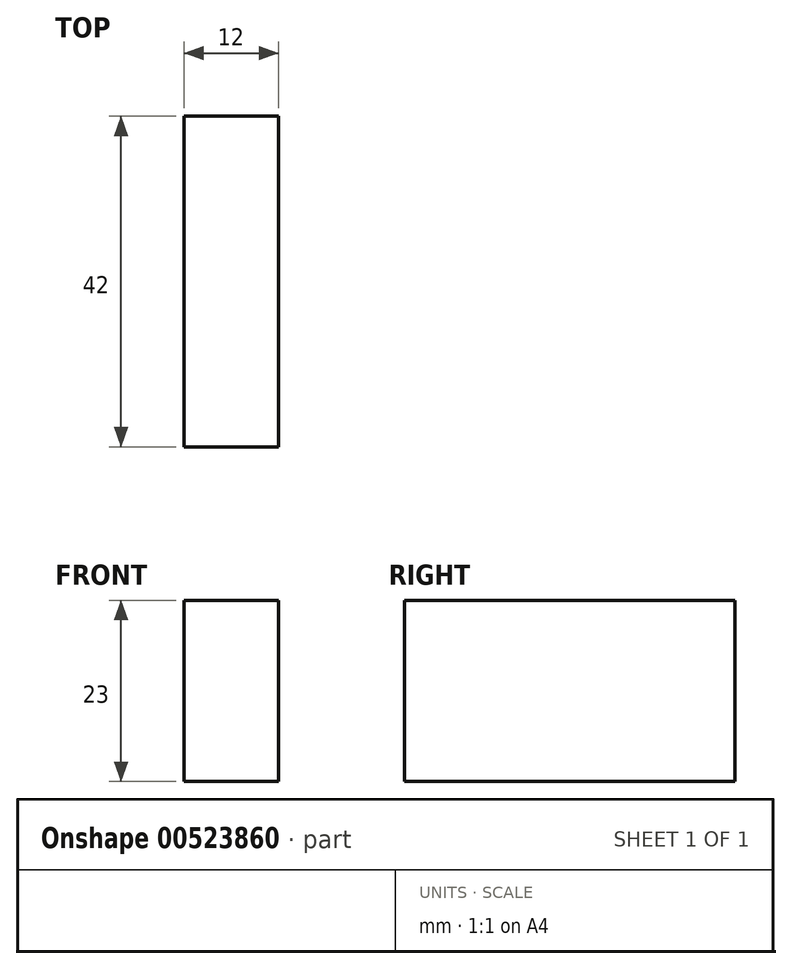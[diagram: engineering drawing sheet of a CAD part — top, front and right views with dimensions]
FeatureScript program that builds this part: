
annotation { "Feature Type Name" : "Feature", "Feature Type Description" : "" }
export const myFeature = defineFeature(function(context is Context, id is Id, definition is map)
    precondition{}
    {
        {
            var Q0;
            Q0=qCreatedBy(makeId("Right.planeOp"),FACE);
            var sketch = newSketch(context, id + "F0", { "sketchPlane" : qUnion([Q0])});
            skLineSegment(sketch, "E0.bottom", {"start": v(-21, 11.5) * mm, "end": v(21, 11.5) * mm});
            skLineSegment(sketch, "E0.top", {"start": v(-21, -11.5) * mm, "end": v(21, -11.5) * mm});
            skLineSegment(sketch, "E0.left", {"start": v(-21, 11.5) * mm, "end": v(-21, -11.5) * mm});
            skLineSegment(sketch, "E0.right", {"start": v(21, 11.5) * mm, "end": v(21, -11.5) * mm});
            skPoint(sketch, "E0.middle", {"position": v(0, 0) * mm});
            skSolve(sketch);
        }
        {
            var Q0;
            Q0=makeQuery(id+"F0.imprint","IMPRINT",FACE,{"disambiguationData":[TD([[makeQuery(id+"F0.imprint","IMPRINT",EDGE,{"derivedFrom":sQuery(id+"F0.wireOp",EDGE,"E0.bottom")}),-1.0]])]});
            extrude(context, id + "F1", {"entities" : qUnion([Q0]), "endBound" : BoundingType.SYMMETRIC, "depth" : 12 * mm, "offsetDistance" : 25 * mm});
        }
    });
